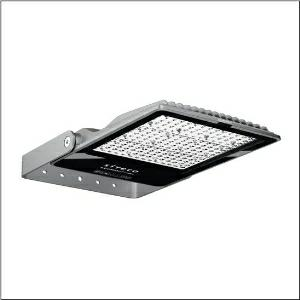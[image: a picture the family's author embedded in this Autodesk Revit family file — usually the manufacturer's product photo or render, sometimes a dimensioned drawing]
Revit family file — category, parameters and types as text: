
# Revit family: sicompact_r__31_midi___pl32_5xa7581e2k23_2195
name_source: partatom
category: Lighting Fixtures
units: mm (PartAtom-declared; Revit-internal decimal feet)

## family parameters
Cut with Voids When Loaded = No
Host = Face
Light Source = No
Part Type = Normal
Room Calculation Point = No
Round Connector Dimension = Use Diameter
Shared = No

## types (1)
- SiCompact® 31 midi  PL32 (1 x LED, 37000 lm, 243 W, 4000K)
    Apparent Load = 243 VA
    CIE Flux Codes = 32 69 98 100 100
    Color Rendering = 70
    Color Temperature = 4000K
    Default Elevation = 1800 mm
    Description = SiCompact® 31 midi, floodlight, primary light control with lens, of plastic, of toughened safety glass, transparent, light distribution: PL32, light emission: direct distribution, primary light characteristic: asymmetric, installation type: surface-mounted, LED, High Power LED, rated luminous flux: 37.000lm, luminous efficacy: 152lm/W, light colour: 740, colour temperature: 4000K, control gear: ECG, with cable, 3x 1.5mm², mains connection: 220..240V, AC, 50/60Hz, connection cable pre-assembled, cable length: 2m, rated input power: 243W, of diecast aluminium, specular, metallic grey (RAL 9006), length: 560mm, width: 330mm, height: 62mm, bracket, of sheet steel, coated, metallic grey (RAL 9006), ON/OFF, protection rating (complete): IP66, insulation class (complete): insulation class I (protective earthing), certification: CE, impact resistance: IK08, permissible operating ambient temperature: -40..+45°C, packaging unit: 1 piece

Light Distribution: PL32
    Height = 62 mm  [stored 0.203412 ft]
    Lamp = 1 x LED
    Lamp Light Flux = 37000 lm
    Lamp Power = 243 W
    Lamp count = 1
    Length = 560 mm
    Luminous efficacy = 152 lm/W
    Manufacturer = Siteco
    ModVariant = No
    Model = 5XA7581E2K23
    Number of Poles = 1
    OnlyDefault = Yes
    Power Factor = 1
    Product Name = SiCompact® 31 midi | PL32
    Product group = floodlight | pylon top
    ProductGroupID = 6101
    Protection Class = Protection class I
    Protection Degree = IP 66
    RLX_Detail_Level = 1
    RlxData = <blob elided: 97829 chars, md5=5b6c1e97>
    Socket = socket
    Standby Power = 0 W
    System Light Flux = 37000 lm
    System Power = 243 W
    Type Comments = Product without accessories
    Type Image = l_1006415.jpg
    URL = http://relux.com
    VarID = ---
    Voltage = 0 V
    Weight = 0.00 kg
    Width = 333 mm

note: [stored X ft] marks values corroborated as IEEE doubles in the binary element streams (Revit-internal decimal feet)

## geometry (parser evidence)
native form markers: Blend x4, Sweep x11
no freeform markers — native parametric forms only
